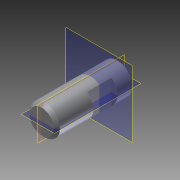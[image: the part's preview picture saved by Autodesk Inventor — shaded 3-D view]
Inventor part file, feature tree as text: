
AUTODESK INVENTOR PART (.ipt)
format: ipt  version: 2011 (Build 150229000, 229)  size: 96,768 bytes
history: native  units: mm (DEFAULTED — no unit token found)
features: extrude x2, sketch x2, chamfer x1, plane x1
ambient origin geometry x8: Origin, YZ Plane, XZ Plane, XY Plane, X Axis, Y Axis, Z Axis, Center Point
feature tree (6):
  extrude  "Extrusion1"  Depth=26.0mm TaperAngle=0.0deg
  chamfer  "Chamfer1"  Distance=1.0mm
  extrude  "Extrusion2"  Depth=8.0mm
  plane  "Work Plane1"
  sketch  "Sketch1"  dims[d0=10.0mm d1=26.0mm d2=0.0mm d3=1.0mm d4=1.0mm]
  sketch  "Sketch2"  dims[d5=2.0mm d6=8.0mm d7=6.0mm d8=26.0mm d9=0.0mm d10=45.0deg]
